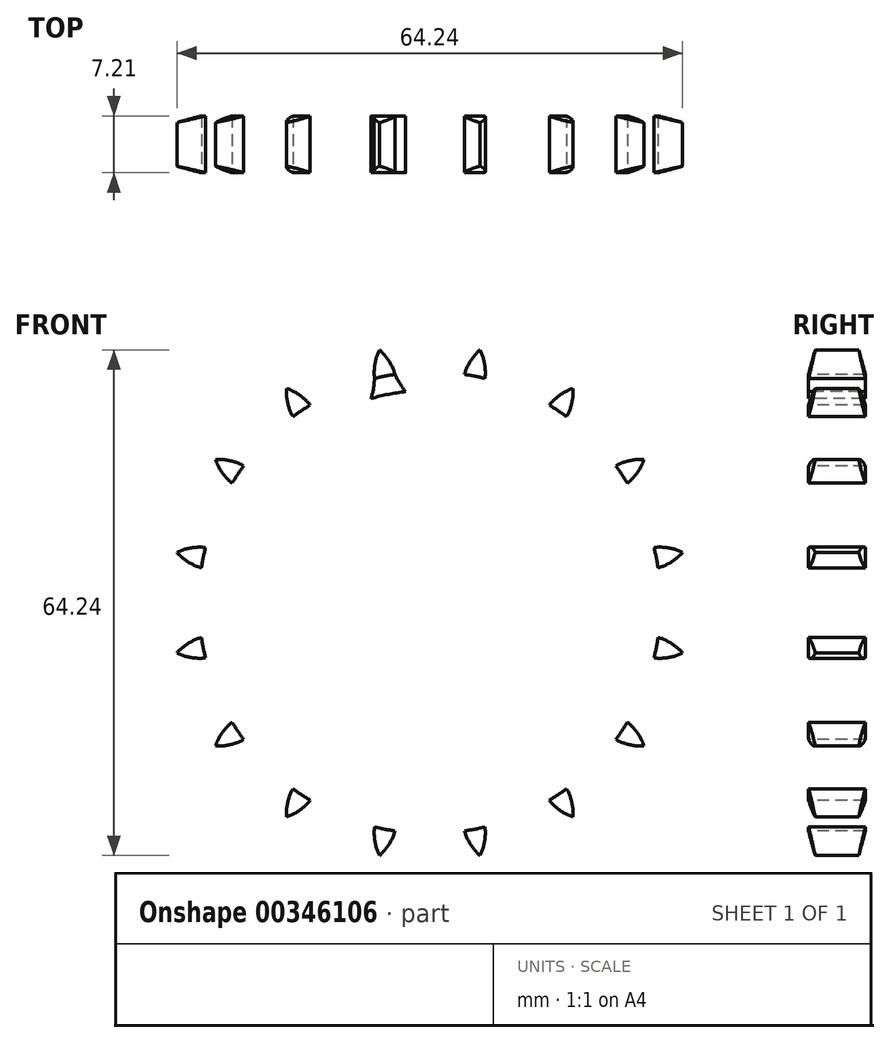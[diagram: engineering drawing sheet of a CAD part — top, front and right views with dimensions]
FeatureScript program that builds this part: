
annotation { "Feature Type Name" : "Feature", "Feature Type Description" : "" }
export const myFeature = defineFeature(function(context is Context, id is Id, definition is map)
    precondition{}
    {
        {
            var Q0;
            Q0=qCreatedBy(makeId("Right.planeOp"),FACE);
            var sketch = newSketch(context, id + "F0", { "sketchPlane" : qUnion([Q0])});
            skLineSegment(sketch, "E0", {"start": v(0, 0) * mm, "end": v(25.64, 0) * mm});
            skLineSegment(sketch, "E1.bottom", {"start": v(0, 7.94) * mm, "end": v(7.21, 7.94) * mm});
            skLineSegment(sketch, "E1.top", {"start": v(0, 35.69) * mm, "end": v(7.21, 35.69) * mm});
            skLineSegment(sketch, "E1.left", {"start": v(0, 7.94) * mm, "end": v(0, 35.69) * mm});
            skLineSegment(sketch, "E1.right", {"start": v(7.21, 7.94) * mm, "end": v(7.21, 35.69) * mm});
            skLineSegment(sketch, "E2.bottom", {"start": v(0, 7.94) * mm, "end": v(22.22, 7.94) * mm});
            skLineSegment(sketch, "E2.top", {"start": v(0, 25.4) * mm, "end": v(22.22, 25.4) * mm});
            skLineSegment(sketch, "E2.left", {"start": v(0, 7.94) * mm, "end": v(0, 25.4) * mm});
            skLineSegment(sketch, "E2.right", {"start": v(22.23, 7.94) * mm, "end": v(22.22, 25.4) * mm});
            skLineSegment(sketch, "E3.MirrorCS", {"start": v(0, -7.94) * mm, "end": v(7.21, -7.94) * mm});
            skLineSegment(sketch, "E4.MirrorCS", {"start": v(22.23, -7.94) * mm, "end": v(22.23, -25.4) * mm});
            skLineSegment(sketch, "E5.MirrorCS", {"start": v(0, -7.94) * mm, "end": v(0, -25.4) * mm});
            skLineSegment(sketch, "E6.MirrorCS", {"start": v(0, -7.94) * mm, "end": v(22.22, -7.94) * mm});
            skLineSegment(sketch, "E7.MirrorCS", {"start": v(0, -25.4) * mm, "end": v(22.22, -25.4) * mm});
            skLineSegment(sketch, "E8.MirrorCS", {"start": v(7.21, -7.94) * mm, "end": v(7.21, -35.69) * mm});
            skLineSegment(sketch, "E9.MirrorCS", {"start": v(0, -35.69) * mm, "end": v(7.21, -35.69) * mm});
            skLineSegment(sketch, "E10.MirrorCS", {"start": v(0, -7.94) * mm, "end": v(0, -35.69) * mm});
            skSolve(sketch);
        }
        {
            var Q0;
            {var subQ5=sQuery(id+"F0.wireOp",EDGE,"E2.right");Q0=makeQuery(id+"F0.imprint","IMPRINT",FACE,{"disambiguationData":[TD([[makeQuery(id+"F0.imprint","IMPRINT",EDGE,{"derivedFrom":subQ5}),1.0]])]});}
            var Q1;
            {var subQ5=sQuery(id+"F0.wireOp",EDGE,"E2.left");Q1=makeQuery(id+"F0.imprint","IMPRINT",FACE,{"disambiguationData":[TD([[makeQuery(id+"F0.imprint","IMPRINT",EDGE,{"derivedFrom":subQ5}),-1.0]])]});}
            var Q2;
            {var subQ0=sQuery(id+"F0.wireOp",EDGE,"E1.top");Q2=makeQuery(id+"F0.imprint","IMPRINT",FACE,{"disambiguationData":[TD([[makeQuery(id+"F0.imprint","IMPRINT",EDGE,{"derivedFrom":subQ0}),-1.0]])]});}
            var Q3;
            Q3=sQuery(id+"F0.wireOp",EDGE,"E0");
            revolve(context, id + "F1", {"entities" : qUnion([Q0, Q1, Q2]), "axis" : qUnion([Q3]), "revolveType" : RevolveType.FULL});
        }
        {
            var Q0;
            Q0=makeQuery(id+"F1.opRevolve","SWEPT_FACE",FACE,{"disambiguationData":[OSD([sQuery(id+"F0.wireOp",EDGE,"E2.top")])]});
            fillet(context, id + "F2", {"entities" : qUnion([Q0]), "radius" : 1.59 * mm, "tangentPropagation" : true, "allowEdgeOverflow" : false});
        }
        {
            var Q0;
            Q0=makeQuery(id+"F1.opRevolve","SWEPT_EDGE",EDGE,{"disambiguationData":[OSD([sQuery(id+"F0.wireOp",EDGE,"E1.top"),sQuery(id+"F0.wireOp",EDGE,"E1.left")])]});
            var Q1;
            Q1=makeQuery(id+"F1.opRevolve","SWEPT_EDGE",EDGE,{"disambiguationData":[OSD([sQuery(id+"F0.wireOp",EDGE,"E1.top"),sQuery(id+"F0.wireOp",EDGE,"E1.right")])]});
            chamfer(context, id + "F3", {"entities" : qUnion([Q0, Q1]), "chamferType" : ChamferType.TWO_OFFSETS, "width1" : 6.35 * mm, "oppositeDirection" : false, "width2" : 1.57 * mm, "tangentPropagation" : true});
        }
        {
            var Q0;
            Q0=makeQuery(id+"F1.opRevolve","SWEPT_FACE",FACE,{"disambiguationData":[OSD([sQuery(id+"F0.wireOp",EDGE,"E1.left"),sQuery(id+"F0.wireOp",EDGE,"E2.left")])]});
            var sketch = newSketch(context, id + "F4", { "sketchPlane" : qUnion([Q0])});
            skCircle(sketch, "E11", {"center": v(0, 0) * mm, "radius": 29.34 * mm, "construction": true});
            skLineSegment(sketch, "E12", {"start": v(0, 0) * mm, "end": v(0, 29.34) * mm});
            skLineSegment(sketch, "E13", {"start": v(41.72, 29.34) * mm, "end": v(0, 29.34) * mm});
            skLineSegment(sketch, "E14", {"start": v(0, 29.34) * mm, "end": v(5, 33.34) * mm});
            skLineSegment(sketch, "E15", {"start": v(5, 33.34) * mm, "end": v(-4.42, 29) * mm, "construction": true});
            skLineSegment(sketch, "E16", {"start": v(12.86, -8.46) * mm, "end": v(-4.42, 29) * mm, "construction": true});
            skArc(sketch, "E17", {"start": v(-8.21, 33.26) * mm, "mid": v(-15.67, 22.8) * mm, "end": v(-4.42, 29) * mm, "construction": true});
            skArc(sketch, "E18", {"start": v(-5.25, 30.81) * mm, "mid": v(-6.55, 32.26) * mm, "end": v(-8.21, 33.26) * mm});
            skArc(sketch, "E19", {"start": v(-4.42, 29) * mm, "mid": v(-4.77, 29.94) * mm, "end": v(-5.25, 30.81) * mm});
            skLineSegment(sketch, "E20", {"start": v(-3.1, 26.86) * mm, "end": v(-3.1, 26.86) * mm});
            skArc(sketch, "E21", {"start": v(-4.42, 29) * mm, "mid": v(-3.82, 27.89) * mm, "end": v(-3.1, 26.86) * mm});
            skArc(sketch, "E22.MirrorCS", {"start": v(4.42, 29) * mm, "mid": v(4.77, 29.94) * mm, "end": v(5.25, 30.81) * mm});
            skArc(sketch, "E23.MirrorCS", {"start": v(5.25, 30.81) * mm, "mid": v(6.55, 32.26) * mm, "end": v(8.21, 33.26) * mm});
            skArc(sketch, "E24.MirrorCS", {"start": v(4.42, 29) * mm, "mid": v(3.82, 27.89) * mm, "end": v(3.1, 26.86) * mm});
            skArc(sketch, "E25", {"start": v(-3.1, 26.86) * mm, "mid": v(13.8, 38.8) * mm, "end": v(-4.42, 29) * mm, "construction": true});
            skArc(sketch, "E26", {"start": v(-0.28, 25.38) * mm, "mid": v(1.84, 32.85) * mm, "end": v(-3.1, 26.86) * mm, "construction": true});
            skArc(sketch, "E27", {"start": v(-0.28, 25.38) * mm, "mid": v(-0.28, 25.38) * mm, "end": v(-0.28, 25.38) * mm});
            skLineSegment(sketch, "E28", {"start": v(0, 0) * mm, "end": v(-8.21, 33.26) * mm, "construction": true});
            skArc(sketch, "E29", {"start": v(-3.1, 26.86) * mm, "mid": v(0, 25.37) * mm, "end": v(3.1, 26.86) * mm});
            skArc(sketch, "E30", {"start": v(3.1, 26.86) * mm, "mid": v(-1.58, 32.97) * mm, "end": v(-0.28, 25.38) * mm, "construction": true});
            skArc(sketch, "E31.1.0", {"start": v(-16.64, 26.46) * mm, "mid": v(-18.4, 27.3) * mm, "end": v(-20.32, 27.59) * mm});
            skArc(sketch, "E31.1.1", {"start": v(-15.18, 25.1) * mm, "mid": v(-15.86, 25.84) * mm, "end": v(-16.64, 26.46) * mm});
            skArc(sketch, "E31.1.2", {"start": v(-15.18, 25.1) * mm, "mid": v(-14.2, 24.3) * mm, "end": v(-13.13, 23.63) * mm});
            skArc(sketch, "E31.1.3", {"start": v(-13.13, 23.63) * mm, "mid": v(-9.71, 23.44) * mm, "end": v(-7.42, 26) * mm});
            skArc(sketch, "E31.1.4", {"start": v(-7.02, 28.49) * mm, "mid": v(-7.14, 27.23) * mm, "end": v(-7.42, 26) * mm});
            skArc(sketch, "E31.1.5", {"start": v(-7.02, 28.49) * mm, "mid": v(-7.05, 29.48) * mm, "end": v(-6.94, 30.48) * mm});
            skArc(sketch, "E31.1.6", {"start": v(-6.94, 30.48) * mm, "mid": v(-6.3, 32.3) * mm, "end": v(-5.14, 33.87) * mm});
            skArc(sketch, "E31.2.0", {"start": v(-25.5, 18.07) * mm, "mid": v(-27.44, 18.18) * mm, "end": v(-29.33, 17.71) * mm});
            skArc(sketch, "E31.2.1", {"start": v(-23.63, 17.38) * mm, "mid": v(-24.54, 17.8) * mm, "end": v(-25.5, 18.07) * mm});
            skArc(sketch, "E31.2.2", {"start": v(-23.63, 17.38) * mm, "mid": v(-22.42, 17.02) * mm, "end": v(-21.18, 16.8) * mm});
            skArc(sketch, "E31.2.3", {"start": v(-21.18, 16.8) * mm, "mid": v(-17.94, 17.94) * mm, "end": v(-16.8, 21.18) * mm});
            skArc(sketch, "E31.2.4", {"start": v(-17.38, 23.63) * mm, "mid": v(-17.02, 22.42) * mm, "end": v(-16.8, 21.18) * mm});
            skArc(sketch, "E31.2.5", {"start": v(-17.38, 23.63) * mm, "mid": v(-17.8, 24.54) * mm, "end": v(-18.07, 25.5) * mm});
            skArc(sketch, "E31.2.6", {"start": v(-18.07, 25.5) * mm, "mid": v(-18.18, 27.44) * mm, "end": v(-17.71, 29.33) * mm});
            skArc(sketch, "E31.3.0", {"start": v(-30.48, 6.94) * mm, "mid": v(-32.3, 6.3) * mm, "end": v(-33.87, 5.14) * mm});
            skArc(sketch, "E31.3.1", {"start": v(-28.49, 7.02) * mm, "mid": v(-29.48, 7.05) * mm, "end": v(-30.48, 6.94) * mm});
            skArc(sketch, "E31.3.2", {"start": v(-28.49, 7.02) * mm, "mid": v(-27.23, 7.14) * mm, "end": v(-26, 7.42) * mm});
            skArc(sketch, "E31.3.3", {"start": v(-26, 7.42) * mm, "mid": v(-23.44, 9.71) * mm, "end": v(-23.63, 13.13) * mm});
            skArc(sketch, "E31.3.4", {"start": v(-25.1, 15.18) * mm, "mid": v(-24.3, 14.2) * mm, "end": v(-23.63, 13.13) * mm});
            skArc(sketch, "E31.3.5", {"start": v(-25.1, 15.18) * mm, "mid": v(-25.84, 15.86) * mm, "end": v(-26.46, 16.64) * mm});
            skArc(sketch, "E31.3.6", {"start": v(-26.46, 16.64) * mm, "mid": v(-27.3, 18.4) * mm, "end": v(-27.59, 20.32) * mm});
            skArc(sketch, "E31.4.0", {"start": v(-30.81, -5.25) * mm, "mid": v(-32.26, -6.55) * mm, "end": v(-33.26, -8.21) * mm});
            skArc(sketch, "E31.4.1", {"start": v(-29, -4.42) * mm, "mid": v(-29.94, -4.77) * mm, "end": v(-30.81, -5.25) * mm});
            skArc(sketch, "E31.4.2", {"start": v(-29, -4.42) * mm, "mid": v(-27.89, -3.82) * mm, "end": v(-26.86, -3.1) * mm});
            skArc(sketch, "E31.4.3", {"start": v(-26.86, -3.1) * mm, "mid": v(-25.37, 0) * mm, "end": v(-26.86, 3.1) * mm});
            skArc(sketch, "E31.4.4", {"start": v(-29, 4.42) * mm, "mid": v(-27.89, 3.82) * mm, "end": v(-26.86, 3.1) * mm});
            skArc(sketch, "E31.4.5", {"start": v(-29, 4.42) * mm, "mid": v(-29.94, 4.77) * mm, "end": v(-30.81, 5.25) * mm});
            skArc(sketch, "E31.4.6", {"start": v(-30.81, 5.25) * mm, "mid": v(-32.26, 6.55) * mm, "end": v(-33.26, 8.21) * mm});
            skArc(sketch, "E31.5.0", {"start": v(-26.46, -16.64) * mm, "mid": v(-27.3, -18.4) * mm, "end": v(-27.59, -20.32) * mm});
            skArc(sketch, "E31.5.1", {"start": v(-25.1, -15.18) * mm, "mid": v(-25.84, -15.86) * mm, "end": v(-26.46, -16.64) * mm});
            skArc(sketch, "E31.5.2", {"start": v(-25.1, -15.18) * mm, "mid": v(-24.3, -14.2) * mm, "end": v(-23.63, -13.13) * mm});
            skArc(sketch, "E31.5.3", {"start": v(-23.63, -13.13) * mm, "mid": v(-23.44, -9.71) * mm, "end": v(-26, -7.42) * mm});
            skArc(sketch, "E31.5.4", {"start": v(-28.49, -7.02) * mm, "mid": v(-27.23, -7.14) * mm, "end": v(-26, -7.42) * mm});
            skArc(sketch, "E31.5.5", {"start": v(-28.49, -7.02) * mm, "mid": v(-29.48, -7.05) * mm, "end": v(-30.48, -6.94) * mm});
            skArc(sketch, "E31.5.6", {"start": v(-30.48, -6.94) * mm, "mid": v(-32.3, -6.3) * mm, "end": v(-33.87, -5.14) * mm});
            skArc(sketch, "E31.6.0", {"start": v(-18.07, -25.5) * mm, "mid": v(-18.18, -27.44) * mm, "end": v(-17.71, -29.33) * mm});
            skArc(sketch, "E31.6.1", {"start": v(-17.38, -23.63) * mm, "mid": v(-17.8, -24.54) * mm, "end": v(-18.07, -25.5) * mm});
            skArc(sketch, "E31.6.2", {"start": v(-17.38, -23.63) * mm, "mid": v(-17.02, -22.42) * mm, "end": v(-16.8, -21.18) * mm});
            skArc(sketch, "E31.6.3", {"start": v(-16.8, -21.18) * mm, "mid": v(-17.94, -17.94) * mm, "end": v(-21.18, -16.8) * mm});
            skArc(sketch, "E31.6.4", {"start": v(-23.63, -17.38) * mm, "mid": v(-22.42, -17.02) * mm, "end": v(-21.18, -16.8) * mm});
            skArc(sketch, "E31.6.5", {"start": v(-23.63, -17.38) * mm, "mid": v(-24.54, -17.8) * mm, "end": v(-25.5, -18.07) * mm});
            skArc(sketch, "E31.6.6", {"start": v(-25.5, -18.07) * mm, "mid": v(-27.44, -18.18) * mm, "end": v(-29.33, -17.71) * mm});
            skArc(sketch, "E31.7.0", {"start": v(-6.94, -30.48) * mm, "mid": v(-6.3, -32.3) * mm, "end": v(-5.14, -33.87) * mm});
            skArc(sketch, "E31.7.1", {"start": v(-7.02, -28.49) * mm, "mid": v(-7.05, -29.48) * mm, "end": v(-6.94, -30.48) * mm});
            skArc(sketch, "E31.7.2", {"start": v(-7.02, -28.49) * mm, "mid": v(-7.14, -27.23) * mm, "end": v(-7.42, -26) * mm});
            skArc(sketch, "E31.7.3", {"start": v(-7.42, -26) * mm, "mid": v(-9.71, -23.44) * mm, "end": v(-13.13, -23.63) * mm});
            skArc(sketch, "E31.7.4", {"start": v(-15.18, -25.1) * mm, "mid": v(-14.2, -24.3) * mm, "end": v(-13.13, -23.63) * mm});
            skArc(sketch, "E31.7.5", {"start": v(-15.18, -25.1) * mm, "mid": v(-15.86, -25.84) * mm, "end": v(-16.64, -26.46) * mm});
            skArc(sketch, "E31.7.6", {"start": v(-16.64, -26.46) * mm, "mid": v(-18.4, -27.3) * mm, "end": v(-20.32, -27.59) * mm});
            skArc(sketch, "E31.8.0", {"start": v(5.25, -30.81) * mm, "mid": v(6.55, -32.26) * mm, "end": v(8.21, -33.26) * mm});
            skArc(sketch, "E31.8.1", {"start": v(4.42, -29) * mm, "mid": v(4.77, -29.94) * mm, "end": v(5.25, -30.81) * mm});
            skArc(sketch, "E31.8.2", {"start": v(4.42, -29) * mm, "mid": v(3.82, -27.89) * mm, "end": v(3.1, -26.86) * mm});
            skArc(sketch, "E31.8.3", {"start": v(3.1, -26.86) * mm, "mid": v(0, -25.37) * mm, "end": v(-3.1, -26.86) * mm});
            skArc(sketch, "E31.8.4", {"start": v(-4.42, -29) * mm, "mid": v(-3.82, -27.89) * mm, "end": v(-3.1, -26.86) * mm});
            skArc(sketch, "E31.8.5", {"start": v(-4.42, -29) * mm, "mid": v(-4.77, -29.94) * mm, "end": v(-5.25, -30.81) * mm});
            skArc(sketch, "E31.8.6", {"start": v(-5.25, -30.81) * mm, "mid": v(-6.55, -32.26) * mm, "end": v(-8.21, -33.26) * mm});
            skArc(sketch, "E31.9.0", {"start": v(16.64, -26.46) * mm, "mid": v(18.4, -27.3) * mm, "end": v(20.32, -27.59) * mm});
            skArc(sketch, "E31.9.1", {"start": v(15.18, -25.1) * mm, "mid": v(15.86, -25.84) * mm, "end": v(16.64, -26.46) * mm});
            skArc(sketch, "E31.9.2", {"start": v(15.18, -25.1) * mm, "mid": v(14.2, -24.3) * mm, "end": v(13.13, -23.63) * mm});
            skArc(sketch, "E31.9.3", {"start": v(13.13, -23.63) * mm, "mid": v(9.71, -23.44) * mm, "end": v(7.42, -26) * mm});
            skArc(sketch, "E31.9.4", {"start": v(7.02, -28.49) * mm, "mid": v(7.14, -27.23) * mm, "end": v(7.42, -26) * mm});
            skArc(sketch, "E31.9.5", {"start": v(7.02, -28.49) * mm, "mid": v(7.05, -29.48) * mm, "end": v(6.94, -30.48) * mm});
            skArc(sketch, "E31.9.6", {"start": v(6.94, -30.48) * mm, "mid": v(6.3, -32.3) * mm, "end": v(5.14, -33.87) * mm});
            skArc(sketch, "E31.10.0", {"start": v(25.5, -18.07) * mm, "mid": v(27.44, -18.18) * mm, "end": v(29.33, -17.71) * mm});
            skArc(sketch, "E31.10.1", {"start": v(23.63, -17.38) * mm, "mid": v(24.54, -17.8) * mm, "end": v(25.5, -18.07) * mm});
            skArc(sketch, "E31.10.2", {"start": v(23.63, -17.38) * mm, "mid": v(22.42, -17.02) * mm, "end": v(21.18, -16.8) * mm});
            skArc(sketch, "E31.10.3", {"start": v(21.18, -16.8) * mm, "mid": v(17.94, -17.94) * mm, "end": v(16.8, -21.18) * mm});
            skArc(sketch, "E31.10.4", {"start": v(17.38, -23.63) * mm, "mid": v(17.02, -22.42) * mm, "end": v(16.8, -21.18) * mm});
            skArc(sketch, "E31.10.5", {"start": v(17.38, -23.63) * mm, "mid": v(17.8, -24.54) * mm, "end": v(18.07, -25.5) * mm});
            skArc(sketch, "E31.10.6", {"start": v(18.07, -25.5) * mm, "mid": v(18.18, -27.44) * mm, "end": v(17.71, -29.33) * mm});
            skArc(sketch, "E31.11.0", {"start": v(30.48, -6.94) * mm, "mid": v(32.3, -6.3) * mm, "end": v(33.87, -5.14) * mm});
            skArc(sketch, "E31.11.1", {"start": v(28.49, -7.02) * mm, "mid": v(29.48, -7.05) * mm, "end": v(30.48, -6.94) * mm});
            skArc(sketch, "E31.11.2", {"start": v(28.49, -7.02) * mm, "mid": v(27.23, -7.14) * mm, "end": v(26, -7.42) * mm});
            skArc(sketch, "E31.11.3", {"start": v(26, -7.42) * mm, "mid": v(23.44, -9.71) * mm, "end": v(23.63, -13.13) * mm});
            skArc(sketch, "E31.11.4", {"start": v(25.1, -15.18) * mm, "mid": v(24.3, -14.2) * mm, "end": v(23.63, -13.13) * mm});
            skArc(sketch, "E31.11.5", {"start": v(25.1, -15.18) * mm, "mid": v(25.84, -15.86) * mm, "end": v(26.46, -16.64) * mm});
            skArc(sketch, "E31.11.6", {"start": v(26.46, -16.64) * mm, "mid": v(27.3, -18.4) * mm, "end": v(27.59, -20.32) * mm});
            skArc(sketch, "E31.12.0", {"start": v(30.81, 5.25) * mm, "mid": v(32.26, 6.55) * mm, "end": v(33.26, 8.21) * mm});
            skArc(sketch, "E31.12.1", {"start": v(29, 4.42) * mm, "mid": v(29.94, 4.77) * mm, "end": v(30.81, 5.25) * mm});
            skArc(sketch, "E31.12.2", {"start": v(29, 4.42) * mm, "mid": v(27.89, 3.82) * mm, "end": v(26.86, 3.1) * mm});
            skArc(sketch, "E31.12.3", {"start": v(26.86, 3.1) * mm, "mid": v(25.37, 0) * mm, "end": v(26.86, -3.1) * mm});
            skArc(sketch, "E31.12.4", {"start": v(29, -4.42) * mm, "mid": v(27.89, -3.82) * mm, "end": v(26.86, -3.1) * mm});
            skArc(sketch, "E31.12.5", {"start": v(29, -4.42) * mm, "mid": v(29.94, -4.77) * mm, "end": v(30.81, -5.25) * mm});
            skArc(sketch, "E31.12.6", {"start": v(30.81, -5.25) * mm, "mid": v(32.26, -6.55) * mm, "end": v(33.26, -8.21) * mm});
            skArc(sketch, "E31.13.0", {"start": v(26.46, 16.64) * mm, "mid": v(27.3, 18.4) * mm, "end": v(27.59, 20.32) * mm});
            skArc(sketch, "E31.13.1", {"start": v(25.1, 15.18) * mm, "mid": v(25.84, 15.86) * mm, "end": v(26.46, 16.64) * mm});
            skArc(sketch, "E31.13.2", {"start": v(25.1, 15.18) * mm, "mid": v(24.3, 14.2) * mm, "end": v(23.63, 13.13) * mm});
            skArc(sketch, "E31.13.3", {"start": v(23.63, 13.13) * mm, "mid": v(23.44, 9.71) * mm, "end": v(26, 7.42) * mm});
            skArc(sketch, "E31.13.4", {"start": v(28.49, 7.02) * mm, "mid": v(27.23, 7.14) * mm, "end": v(26, 7.42) * mm});
            skArc(sketch, "E31.13.5", {"start": v(28.49, 7.02) * mm, "mid": v(29.48, 7.05) * mm, "end": v(30.48, 6.94) * mm});
            skArc(sketch, "E31.13.6", {"start": v(30.48, 6.94) * mm, "mid": v(32.3, 6.3) * mm, "end": v(33.87, 5.14) * mm});
            skArc(sketch, "E31.14.0", {"start": v(18.07, 25.5) * mm, "mid": v(18.18, 27.44) * mm, "end": v(17.71, 29.33) * mm});
            skArc(sketch, "E31.14.1", {"start": v(17.38, 23.63) * mm, "mid": v(17.8, 24.54) * mm, "end": v(18.07, 25.5) * mm});
            skArc(sketch, "E31.14.2", {"start": v(17.38, 23.63) * mm, "mid": v(17.02, 22.42) * mm, "end": v(16.8, 21.18) * mm});
            skArc(sketch, "E31.14.3", {"start": v(16.8, 21.18) * mm, "mid": v(17.94, 17.94) * mm, "end": v(21.18, 16.8) * mm});
            skArc(sketch, "E31.14.4", {"start": v(23.63, 17.38) * mm, "mid": v(22.42, 17.02) * mm, "end": v(21.18, 16.8) * mm});
            skArc(sketch, "E31.14.5", {"start": v(23.63, 17.38) * mm, "mid": v(24.54, 17.8) * mm, "end": v(25.5, 18.07) * mm});
            skArc(sketch, "E31.14.6", {"start": v(25.5, 18.07) * mm, "mid": v(27.44, 18.18) * mm, "end": v(29.33, 17.71) * mm});
            skArc(sketch, "E31.15.0", {"start": v(6.94, 30.48) * mm, "mid": v(6.3, 32.3) * mm, "end": v(5.14, 33.87) * mm});
            skArc(sketch, "E31.15.1", {"start": v(7.02, 28.49) * mm, "mid": v(7.05, 29.48) * mm, "end": v(6.94, 30.48) * mm});
            skArc(sketch, "E31.15.2", {"start": v(7.02, 28.49) * mm, "mid": v(7.14, 27.23) * mm, "end": v(7.42, 26) * mm});
            skArc(sketch, "E31.15.3", {"start": v(7.42, 26) * mm, "mid": v(9.71, 23.44) * mm, "end": v(13.13, 23.63) * mm});
            skArc(sketch, "E31.15.4", {"start": v(15.18, 25.1) * mm, "mid": v(14.2, 24.3) * mm, "end": v(13.13, 23.63) * mm});
            skArc(sketch, "E31.15.5", {"start": v(15.18, 25.1) * mm, "mid": v(15.86, 25.84) * mm, "end": v(16.64, 26.46) * mm});
            skArc(sketch, "E31.15.6", {"start": v(16.64, 26.46) * mm, "mid": v(18.4, 27.3) * mm, "end": v(20.32, 27.59) * mm});
            skSolve(sketch);
        }
        {
            var Q0;
            {var subQ5=sQuery(id+"F4.wireOp",EDGE,"E31.15.1");var subQ7=sQuery(id+"F4.wireOp",EDGE,"E13");var subQ9=makeQuery(id+"F4.imprint","INTERSECT",VERTEX,{"derivedFrom":[subQ7,subQ5]});Q0=makeQuery(id+"F4.imprint","IMPRINT",FACE,{"disambiguationData":[TD([[makeQuery(id+"F4.imprint","IMPRINT",EDGE,{"disambiguationData":[TD([[subQ9,-1.0]])],"derivedFrom":subQ7}),-1.0]])]});}
            var Q1;
            Q1=makeQuery(id+"F4.imprint","IMPRINT",FACE,{"disambiguationData":[TD([[makeQuery(id+"F4.imprint","IMPRINT",EDGE,{"derivedFrom":makeQuery(id+"F1.opRevolve","SWEPT_EDGE",EDGE,{"disambiguationData":[OSD([sQuery(id+"F0.wireOp",EDGE,"E2.bottom"),sQuery(id+"F0.wireOp",EDGE,"E2.left")])]})}),1.0]])]});
            var Q2;
            {var subQ4=sQuery(id+"F4.wireOp",EDGE,"E19");Q2=makeQuery(id+"F4.imprint","IMPRINT",FACE,{"disambiguationData":[TD([[makeQuery(id+"F4.imprint","IMPRINT",EDGE,{"derivedFrom":subQ4}),1.0]])]});}
            var Q3;
            {var subQ4=sQuery(id+"F4.wireOp",EDGE,"E31.1.1");Q3=makeQuery(id+"F4.imprint","IMPRINT",FACE,{"disambiguationData":[TD([[makeQuery(id+"F4.imprint","IMPRINT",EDGE,{"derivedFrom":subQ4}),1.0]])]});}
            var Q4;
            {var subQ4=sQuery(id+"F4.wireOp",EDGE,"E31.2.1");Q4=makeQuery(id+"F4.imprint","IMPRINT",FACE,{"disambiguationData":[TD([[makeQuery(id+"F4.imprint","IMPRINT",EDGE,{"derivedFrom":subQ4}),1.0]])]});}
            var Q5;
            {var subQ4=sQuery(id+"F4.wireOp",EDGE,"E31.3.1");Q5=makeQuery(id+"F4.imprint","IMPRINT",FACE,{"disambiguationData":[TD([[makeQuery(id+"F4.imprint","IMPRINT",EDGE,{"derivedFrom":subQ4}),1.0]])]});}
            var Q6;
            {var subQ4=sQuery(id+"F4.wireOp",EDGE,"E31.4.1");Q6=makeQuery(id+"F4.imprint","IMPRINT",FACE,{"disambiguationData":[TD([[makeQuery(id+"F4.imprint","IMPRINT",EDGE,{"derivedFrom":subQ4}),1.0]])]});}
            var Q7;
            {var subQ4=sQuery(id+"F4.wireOp",EDGE,"E31.5.1");Q7=makeQuery(id+"F4.imprint","IMPRINT",FACE,{"disambiguationData":[TD([[makeQuery(id+"F4.imprint","IMPRINT",EDGE,{"derivedFrom":subQ4}),1.0]])]});}
            var Q8;
            {var subQ4=sQuery(id+"F4.wireOp",EDGE,"E31.6.1");Q8=makeQuery(id+"F4.imprint","IMPRINT",FACE,{"disambiguationData":[TD([[makeQuery(id+"F4.imprint","IMPRINT",EDGE,{"derivedFrom":subQ4}),1.0]])]});}
            var Q9;
            {var subQ4=sQuery(id+"F4.wireOp",EDGE,"E31.7.1");Q9=makeQuery(id+"F4.imprint","IMPRINT",FACE,{"disambiguationData":[TD([[makeQuery(id+"F4.imprint","IMPRINT",EDGE,{"derivedFrom":subQ4}),1.0]])]});}
            var Q10;
            {var subQ4=sQuery(id+"F4.wireOp",EDGE,"E31.8.1");Q10=makeQuery(id+"F4.imprint","IMPRINT",FACE,{"disambiguationData":[TD([[makeQuery(id+"F4.imprint","IMPRINT",EDGE,{"derivedFrom":subQ4}),1.0]])]});}
            var Q11;
            {var subQ4=sQuery(id+"F4.wireOp",EDGE,"E31.9.1");Q11=makeQuery(id+"F4.imprint","IMPRINT",FACE,{"disambiguationData":[TD([[makeQuery(id+"F4.imprint","IMPRINT",EDGE,{"derivedFrom":subQ4}),1.0]])]});}
            var Q12;
            {var subQ4=sQuery(id+"F4.wireOp",EDGE,"E31.10.1");Q12=makeQuery(id+"F4.imprint","IMPRINT",FACE,{"disambiguationData":[TD([[makeQuery(id+"F4.imprint","IMPRINT",EDGE,{"derivedFrom":subQ4}),1.0]])]});}
            var Q13;
            {var subQ4=sQuery(id+"F4.wireOp",EDGE,"E31.11.1");Q13=makeQuery(id+"F4.imprint","IMPRINT",FACE,{"disambiguationData":[TD([[makeQuery(id+"F4.imprint","IMPRINT",EDGE,{"derivedFrom":subQ4}),1.0]])]});}
            var Q14;
            {var subQ4=sQuery(id+"F4.wireOp",EDGE,"E31.12.1");Q14=makeQuery(id+"F4.imprint","IMPRINT",FACE,{"disambiguationData":[TD([[makeQuery(id+"F4.imprint","IMPRINT",EDGE,{"derivedFrom":subQ4}),1.0]])]});}
            var Q15;
            {var subQ4=sQuery(id+"F4.wireOp",EDGE,"E31.13.1");Q15=makeQuery(id+"F4.imprint","IMPRINT",FACE,{"disambiguationData":[TD([[makeQuery(id+"F4.imprint","IMPRINT",EDGE,{"derivedFrom":subQ4}),1.0]])]});}
            var Q16;
            {var subQ4=sQuery(id+"F4.wireOp",EDGE,"E31.14.1");Q16=makeQuery(id+"F4.imprint","IMPRINT",FACE,{"disambiguationData":[TD([[makeQuery(id+"F4.imprint","IMPRINT",EDGE,{"derivedFrom":subQ4}),1.0]])]});}
            var Q17;
            {var subQ0=sQuery(id+"F4.wireOp",EDGE,"E31.15.1");var subQ1=sQuery(id+"F4.wireOp",EDGE,"E13");var subQ2=makeQuery(id+"F4.imprint","INTERSECT",VERTEX,{"derivedFrom":[subQ1,subQ0]});Q17=makeQuery(id+"F4.imprint","IMPRINT",FACE,{"disambiguationData":[TD([[makeQuery(id+"F4.imprint","IMPRINT",EDGE,{"disambiguationData":[TD([[subQ2,-1.0]])],"derivedFrom":subQ1}),1.0]])]});}
            var Q18;
            {var subQ1=sQuery(id+"F4.wireOp",EDGE,"E21");Q18=makeQuery(id+"F4.imprint","IMPRINT",FACE,{"disambiguationData":[TD([[makeQuery(id+"F4.imprint","IMPRINT",EDGE,{"derivedFrom":subQ1}),-1.0]])]});}
            extrude(context, id + "F5", {"entities" : qUnion([Q0, Q1, Q2, Q3, Q4, Q5, Q6, Q7, Q8, Q9, Q10, Q11, Q12, Q13, Q14, Q15, Q16, Q17, Q18]), "operationType" : NewBodyOperationType.INTERSECT, "endBound" : BoundingType.THROUGH_ALL, "oppositeDirection" : true, "depth" : 25.4 * mm});
        }
    });
